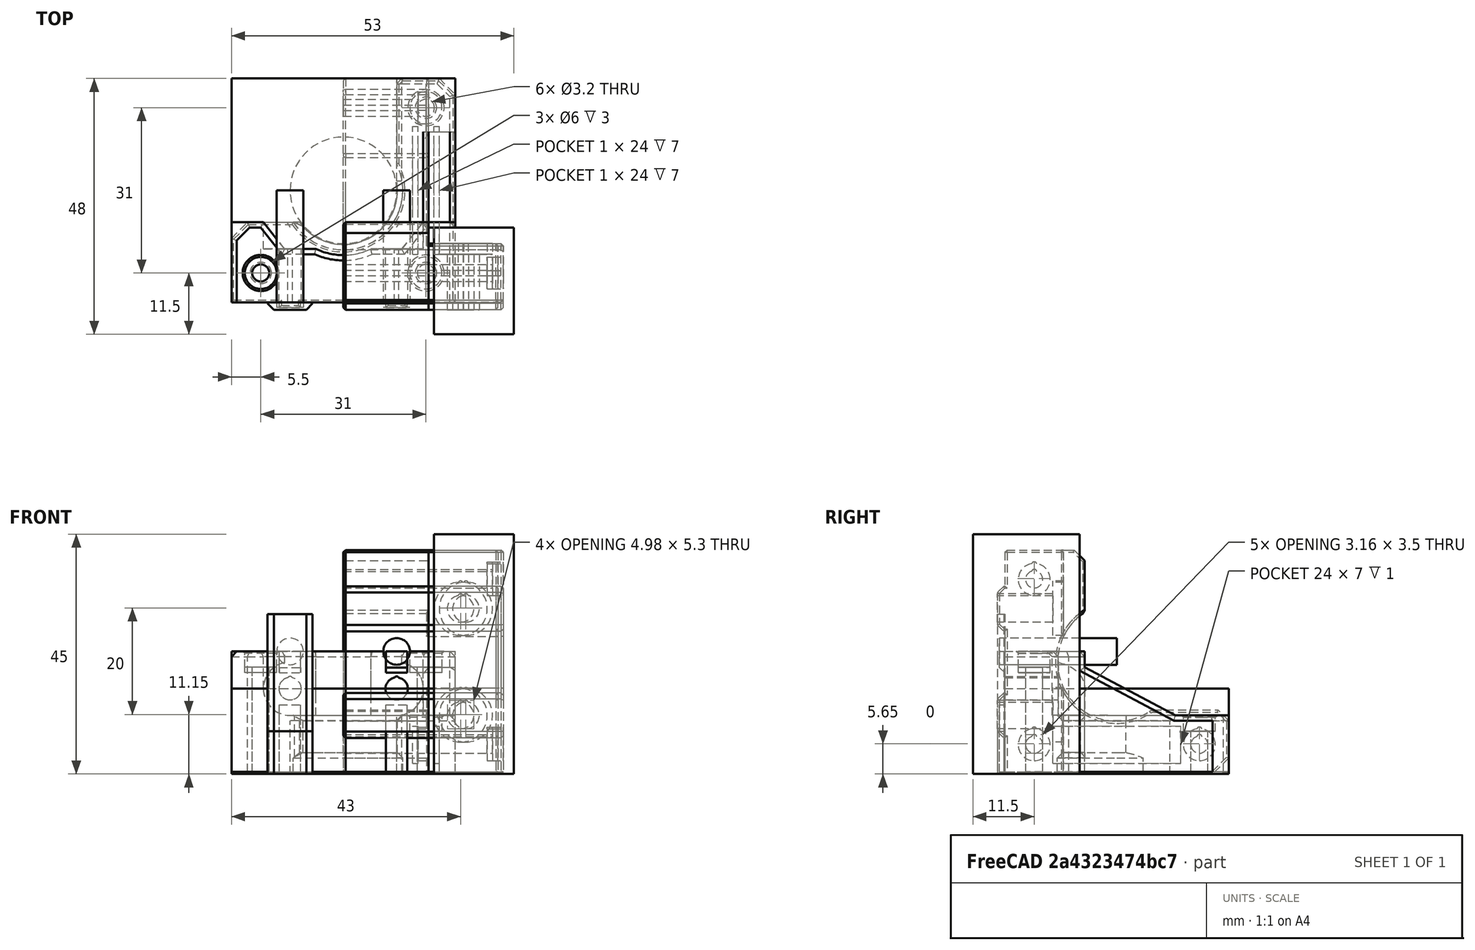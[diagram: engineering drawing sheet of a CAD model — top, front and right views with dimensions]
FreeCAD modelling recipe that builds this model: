
FCSTD DOCUMENT  (FreeCAD 0.18R14555 (Git shallow))
Label: Y-motor-mount
License: All rights reserved
LicenseURL: http://en.wikipedia.org/wiki/All_rights_reserved
objects: Part::Box×22, Part::Cylinder×22, Part::MultiFuse×19, Part::Cut×12, Part::Chamfer×10, Part::Feature×8, Part::MultiCommon×2, Part::Fillet×2
note: 97 computed .brp shape members not serialized (recipe doc carries the construction recipe); baked Part::Feature solids carry a one-line shape summary decoded from their .brp

FEATURE [Part::Box] Box  label="Cube"
  AttacherType = Attacher::AttachEngine3D
  Height = 16
  Length = 42
  Placement = pos=(-21,-21,0) rot=(0,0,1;0rad)
  Width = 42
FEATURE [Part::Cylinder] Cylinder
  Angle = 360
  AttacherType = Attacher::AttachEngine3D
  Height = 4
  Radius = 11.15
FEATURE [Part::Cylinder] Cylinder001
  Angle = 360
  AttacherType = Attacher::AttachEngine3D
  Height = 5
  Placement = pos=(-15.5,-15.5,28) rot=(0,0,1;0rad)
  Radius = 3
FEATURE [Part::Cylinder] Cylinder002
  Angle = 360
  AttacherType = Attacher::AttachEngine3D
  Height = 5
  Placement = pos=(15.5,15.5,8) rot=(0,0,1;0rad)
  Radius = 3
FEATURE [Part::Cylinder] Cylinder003
  Angle = 360
  AttacherType = Attacher::AttachEngine3D
  Height = 5
  Placement = pos=(15.5,-15.5,28) rot=(0,0,1;0rad)
  Radius = 3
FEATURE [Part::Box] Box001  label="Cube001"
  AttacherType = Attacher::AttachEngine3D
  Height = 30
  Length = 42
  Placement = pos=(-21,-21,0) rot=(0,0,1;0rad)
  Width = 15
FEATURE [Part::Box] Box002  label="Cube002"
  AttacherType = Attacher::AttachEngine3D
  Height = 16
  Length = 11
  Placement = pos=(10,-21,0) rot=(0,0,1;0rad)
  Width = 42
FEATURE [Part::Box] Box003  label="Cube003"
  AttacherType = Attacher::AttachEngine3D
  Height = 16
  Length = 42
  Placement = pos=(-21,-21,0) rot=(0,0,1;0rad)
  Width = 15
FEATURE [Part::Cylinder] Cylinder006
  Angle = 360
  AttacherType = Attacher::AttachEngine3D
  Height = 40
  Placement = pos=(-15.5,-15.5,0) rot=(0,0,1;0rad)
  Radius = 1.6
FEATURE [Part::Cylinder] Cylinder007
  Angle = 360
  AttacherType = Attacher::AttachEngine3D
  Height = 40
  Placement = pos=(15.5,-15.5,0) rot=(0,0,1;0rad)
  Radius = 1.6
FEATURE [Part::Cylinder] Cylinder008
  Angle = 360
  AttacherType = Attacher::AttachEngine3D
  Height = 40
  Placement = pos=(15.5,15.5,0) rot=(0,0,1;0rad)
  Radius = 1.6
FEATURE [Part::MultiFuse] Fusion001
  Shapes = -> [Cylinder006,Cylinder007,Cylinder008]
FEATURE [Part::Cylinder] Cylinder011
  Angle = 360
  AttacherType = Attacher::AttachEngine3D
  Height = 22
  Placement = pos=(-10,5.1e-15,23) rot=(1,0,0;1.5708rad)
  Radius = 2.5
FEATURE [Part::Cylinder] Cylinder012
  Angle = 360
  AttacherType = Attacher::AttachEngine3D
  Height = 10
  Placement = pos=(10,-10,23) rot=(1,0,0;1.5708rad)
  Radius = 5
FEATURE [Part::Cylinder] Cylinder013
  Angle = 360
  AttacherType = Attacher::AttachEngine3D
  Height = 22
  Placement = pos=(10,5.1e-15,23) rot=(1,0,0;1.5708rad)
  Radius = 2.5
FEATURE [Part::Cylinder] Cylinder014
  Angle = 360
  AttacherType = Attacher::AttachEngine3D
  Height = 10
  Placement = pos=(-10,-10,23) rot=(1,0,0;1.5708rad)
  Radius = 5
FEATURE [Part::MultiFuse] Fusion003
  Shapes = -> [Cylinder013,Cylinder011]
FEATURE [Part::Feature] Part__Feature  label="y_motor_mount v18"
  shape: bbox 62 x 21 x 44 mm, 162 faces (baked)
FEATURE [Part::Box] Box004  label="Cube004"
  AttacherType = Attacher::AttachEngine3D
  Height = 10
  Length = 10
  Placement = pos=(-15.5,-6,8) rot=(0,0,1;0rad)
  Width = 8
FEATURE [Part::MultiCommon] Common
  Placement = pos=(3.5,-15.5,2) rot=(0.57735,0.57735,-0.57735;4.18879rad)
  Shapes = -> [Part__Feature,Box004]
FEATURE [Part::Feature] Common001
  Placement = pos=(3.5,-15.5,2) rot=(0.57735,0.57735,-0.57735;4.18879rad)
  shape: bbox 8.45 x 1.4 x 8 mm, 8 faces (baked)
FEATURE [Part::Feature] Common002
  Placement = pos=(3.5,-15.5,24) rot=(0.57735,0.57735,-0.57735;4.18879rad)
  shape: bbox 8.45 x 1.4 x 8 mm, 8 faces (baked)
FEATURE [Part::Feature] Common003
  Placement = pos=(3.5,-15.5,16) rot=(0.57735,0.57735,-0.57735;4.18879rad)
  shape: bbox 8.45 x 1.4 x 8 mm, 8 faces (baked)
FEATURE [Part::Feature] Common004
  Placement = pos=(3.5,-15.5,9) rot=(0.57735,0.57735,-0.57735;4.18879rad)
  shape: bbox 8.45 x 1.4 x 8 mm, 8 faces (baked)
FEATURE [Part::MultiFuse] Fusion005
  Shapes = -> [Common002,Common003,Common004,Common001]
FEATURE [Part::Feature] Chamfer002001  label="Chamfer003"
  Placement = pos=(-5e-15,0,21) rot=(0,1,0;1.5708rad)
  shape: bbox 30.28 x 43.4 x 42 mm, 123 faces (baked)
FEATURE [Part::Box] Box005  label="Cube005"
  AttacherType = Attacher::AttachEngine3D
  Height = 45
  Length = 15
  Placement = pos=(17,-27,0) rot=(0,0,1;0rad)
  Width = 20
FEATURE [Part::Feature] Chamfer002002  label="Chamfer004"
  Placement = pos=(-5e-15,0,21) rot=(0,1,0;1.5708rad)
  shape: bbox 30.28 x 43.4 x 42 mm, 123 faces (baked)
FEATURE [Part::Box] Box006  label="Cube006"
  AttacherType = Attacher::AttachEngine3D
  Height = 45
  Length = 15
  Placement = pos=(17,-27,0) rot=(0,0,1;0rad)
  Width = 20
FEATURE [Part::MultiCommon] Common005
  Placement = pos=(-1,0,0) rot=(0,0,1;0rad)
  Shapes = -> [Box006,Chamfer002002]
FEATURE [Part::Cylinder] Cylinder023
  Angle = 360
  AttacherType = Attacher::AttachEngine3D
  Height = 30
  Radius = 10.15
FEATURE [Part::MultiFuse] Fusion005006
  Shapes = -> [Cylinder023,Cylinder]
FEATURE [Part::Chamfer] Chamfer002003
  Base = -> Fusion005006
  Edges = 1 edges r=0.99: [Edge4]
FEATURE [Part::Cylinder] Cylinder024
  Angle = 360
  AttacherType = Attacher::AttachEngine3D
  Height = 39
  Radius = 12.15
FEATURE [Part::Cut] Cut
  Base = -> Box001
  Placement = pos=(0,0,-2) rot=(0,0,1;0rad)
  Tool = -> Cylinder024
FEATURE [Part::Cylinder] Cylinder025
  Angle = 360
  AttacherType = Attacher::AttachEngine3D
  Height = 10
  Radius = 10
FEATURE [Part::MultiFuse] Fusion
  Shapes = -> [Box002,Box003]
FEATURE [Part::Chamfer] Chamfer
  Base = -> Fusion
  Edges = 1 edges r=5: [Edge17]
FEATURE [Part::Cylinder] Cylinder028
  Angle = 360
  AttacherType = Attacher::AttachEngine3D
  Height = 10
  Placement = pos=(10,-20,27.7) rot=(-1,0,0;1.5708rad)
  Radius = 0.5
FEATURE [Part::Cylinder] Cylinder029
  Angle = 360
  AttacherType = Attacher::AttachEngine3D
  Height = 10
  Placement = pos=(-10,-20,27.7) rot=(-1,0,0;1.5708rad)
  Radius = 0.5
FEATURE [Part::MultiFuse] Fusion005008
  Placement = pos=(0,9,-7) rot=(0,0,1;0rad)
  Shapes = -> [Cylinder012,Cylinder028,Cylinder014,Cylinder029]
FEATURE [Part::MultiFuse] Fusion005010
  Placement = pos=(0,0,-8) rot=(0,0,1;0rad)
  Shapes = -> [Cylinder001,Cylinder003]
FEATURE [Part::Box] Box007  label="Cube007"
  AttacherType = Attacher::AttachEngine3D
  Height = 7
  Length = 42
  Placement = pos=(-21,-26,-2) rot=(0,0,1;0rad)
  Width = 47
FEATURE [Part::Box] Box008  label="Cube008"
  AttacherType = Attacher::AttachEngine3D
  Height = 16
  Length = 30
  Placement = pos=(-15,-11,18) rot=(0,0,1;0rad)
  Width = 10
FEATURE [Part::Fillet] Fillet
  Base = -> Box008
  Edges = 2 edges r=5: [Edge4,Edge8]
FEATURE [Part::Box] Box009  label="Cube009"
  AttacherType = Attacher::AttachEngine3D
  Height = 7
  Length = 3
  Placement = pos=(-11,-11,27) rot=(0,0,1;0rad)
  Width = 10
FEATURE [Part::Box] Box010  label="Cube010"
  AttacherType = Attacher::AttachEngine3D
  Height = 7
  Length = 3
  Placement = pos=(8,-11,27) rot=(0,0,1;0rad)
  Width = 10
FEATURE [Part::Box] Box011  label="Cube011"
  AttacherType = Attacher::AttachEngine3D
  Height = 6
  Length = 7
  Placement = pos=(8,-11,28) rot=(0,0,1;0rad)
  Width = 10
FEATURE [Part::Box] Box012  label="Cube012"
  AttacherType = Attacher::AttachEngine3D
  Height = 6
  Length = 7
  Placement = pos=(-15,-11,28) rot=(0,0,1;0rad)
  Width = 10
FEATURE [Part::MultiFuse] Fusion005013
  Shapes = -> [Box012,Box011]
FEATURE [Part::Cut] Cut007
  Base = -> Fillet
  Tool = -> Fusion005013
FEATURE [Part::Fillet] Fillet001
  Base = -> Cut007
  Edges = 2 edges r=4.99: [Edge2,Edge27]
FEATURE [Part::MultiFuse] Fusion005014
  Placement = pos=(0,0,-7) rot=(0,0,1;0rad)
  Shapes = -> [Fillet001,Box009,Box010]
FEATURE [Part::Cylinder] Cylinder030
  Angle = 360
  AttacherType = Attacher::AttachEngine3D
  Height = 20
  Placement = pos=(10,-21,18) rot=(-1,0,0;1.5708rad)
  Radius = 2.1
FEATURE [Part::Cylinder] Cylinder031
  Angle = 360
  AttacherType = Attacher::AttachEngine3D
  Height = 20
  Placement = pos=(-10,-21,18) rot=(-1,0,0;1.5708rad)
  Radius = 2.1
FEATURE [Part::Cylinder] Cylinder032
  Angle = 360
  AttacherType = Attacher::AttachEngine3D
  Height = 20
  Placement = pos=(10,-21,19.8) rot=(-1,0,0;1.5708rad)
  Radius = 0.5
FEATURE [Part::Cylinder] Cylinder033
  Angle = 360
  AttacherType = Attacher::AttachEngine3D
  Height = 20
  Placement = pos=(-10,-21,19.8) rot=(-1,0,0;1.5708rad)
  Radius = 0.5
FEATURE [Part::MultiFuse] Fusion005016
  Placement = pos=(0,0,-2) rot=(0,0,1;0rad)
  Shapes = -> [Cylinder033,Cylinder030,Cylinder032,Cylinder031]
FEATURE [Part::Box] Box014  label="Cube014"
  AttacherType = Attacher::AttachEngine3D
  Height = 13
  Length = 4
  Placement = pos=(8,-22,0) rot=(0,0,1;0rad)
  Width = 1
FEATURE [Part::Box] Box015  label="Cube015"
  AttacherType = Attacher::AttachEngine3D
  Height = 13
  Length = 4
  Placement = pos=(-12,-22,0) rot=(0,0,1;0rad)
  Width = 1
FEATURE [Part::Box] Box016  label="Cube016"
  AttacherType = Attacher::AttachEngine3D
  Height = 4
  Length = 4
  Placement = pos=(8,-22,21) rot=(0,0,1;0rad)
  Width = 1
FEATURE [Part::Box] Box017  label="Cube017"
  AttacherType = Attacher::AttachEngine3D
  Height = 4
  Length = 4
  Placement = pos=(-12,-22,21) rot=(0,0,1;0rad)
  Width = 1
FEATURE [Part::Chamfer] Chamfer002006
  Base = -> Box017
  Edges = 1 edges r=0.99: [Edge9]
  Placement = pos=(0,0,-2) rot=(0,0,1;0rad)
FEATURE [Part::Chamfer] Chamfer002007
  Base = -> Box016
  Edges = 1 edges r=0.99: [Edge9]
  Placement = pos=(0,0,-2) rot=(0,0,1;0rad)
FEATURE [Part::Box] Box018  label="Cube018"
  AttacherType = Attacher::AttachEngine3D
  Height = 7
  Length = 1
  Placement = pos=(13,-12,2) rot=(0,0,1;0rad)
  Width = 24
FEATURE [Part::Box] Box019  label="Cube019"
  AttacherType = Attacher::AttachEngine3D
  Height = 7
  Length = 1
  Placement = pos=(17,-12,2) rot=(0,0,1;0rad)
  Width = 24
FEATURE [Part::MultiFuse] Fusion005018002  label="selective-infill"
  Shapes = -> [Box018,Box019]
FEATURE [Part::MultiFuse] Fusion005018004
  Shapes = -> [Chamfer,Cut]
FEATURE [Part::Cut] Cut008
  Base = -> Fusion005018004
  Placement = pos=(0,0,-5) rot=(0,0,1;0rad)
  Tool = -> Box007
FEATURE [Part::Cut] Cut009
  Base = -> Cut008
  Tool = -> Chamfer002003
FEATURE [Part::Cut] Cut010
  Base = -> Cut009
  Tool = -> Cylinder002
FEATURE [Part::Cut] Cut011
  Base = -> Cut010
  Tool = -> Fusion005010
FEATURE [Part::Cut] Cut012
  Base = -> Cut011
  Tool = -> Fusion001
FEATURE [Part::Cut] Cut013
  Base = -> Cut012
  Tool = -> Fusion005008
FEATURE [Part::Cut] Cut014
  Base = -> Cut013
  Tool = -> Fusion005016
FEATURE [Part::Box] Box020  label="Cube020"
  AttacherType = Attacher::AttachEngine3D
  Height = 10
  Length = 6
  Placement = pos=(15,-7,10) rot=(0,0,1;0rad)
  Width = 18
FEATURE [Part::Box] Box021  label="Cube021"
  AttacherType = Attacher::AttachEngine3D
  Height = 10
  Length = 10
  Placement = pos=(5,-11,16) rot=(0,0,1;0rad)
  Width = 10
FEATURE [Part::Box] Box022  label="Cube022"
  AttacherType = Attacher::AttachEngine3D
  Height = 10
  Length = 10
  Placement = pos=(-15,-11,16) rot=(0,0,1;0rad)
  Width = 10
FEATURE [Part::Chamfer] Chamfer002010
  Base = -> Box021
  Edges = 1 edges: [Edge5 r1=5 r2=4]
FEATURE [Part::Chamfer] Chamfer002011
  Base = -> Box022
  Edges = 1 edges: [Edge1 r1=5 r2=4]
FEATURE [Part::MultiFuse] Fusion005018006002
  Shapes = -> [Chamfer002010,Chamfer002011]
FEATURE [Part::MultiFuse] Fusion005018006003
  Shapes = -> [Fusion005018006002]
FEATURE [Part::MultiFuse] Fusion005018006004
  Shapes = -> [Fusion005018006003]
FEATURE [Part::MultiFuse] Fusion005018006005
  Shapes = -> [Fusion005018006004,Fusion005014]
FEATURE [Part::MultiFuse] Fusion005018006006
  Shapes = -> [Box014,Box015,Chamfer002006,Chamfer002007]
FEATURE [Part::Cut] Cut015
  Base = -> Cut014
  Tool = -> Fusion005018006005
FEATURE [Part::Chamfer] Chamfer002012
  Base = -> Box020
  Edges = 1 edges: [Edge12 r1=9 r2=17]
FEATURE [Part::MultiFuse] Fusion005018006007
  Shapes = -> [Fusion005018006006,Cut015,Chamfer002012]
FEATURE [Part::Feature] Fusion005018006007001  label="Fusion005018006008"
  shape: bbox 42 x 43 x 23 mm, 61 faces (baked)
FEATURE [Part::Chamfer] Chamfer002013
  Base = -> Fusion005018006007001
  Edges = 2 edges r=3: [Edge90,Edge151]
FEATURE [Part::Chamfer] Chamfer002014
  Base = -> Chamfer002013
  Edges = 23 edges r=1: [Edge22,Edge26,Edge50,Edge55,Edge67,Edge68,Edge72,Edge77,Edge80,Edge81,Edge82,Edge83,Edge91,Edge92,Edge93,Edge95,Edge97,Edge99,Edge142,Edge143,Edge144,Edge145,Edge159]
FEATURE [Part::Chamfer] Chamfer002015
  Base = -> Chamfer002014
  Edges = 25 edges r=0.4: [Edge1,Edge2,Edge3,Edge4,Edge5,Edge6,Edge7,Edge8,Edge9,Edge10,Edge11,Edge12,Edge13,Edge14,Edge15,Edge16,Edge17,Edge18,Edge19,Edge20,Edge21,Edge22,Edge145,Edge168,Edge169]
FEATURE [Part::Cut] Cut016
  Base = -> Chamfer002015
  Tool = -> Fusion005018002
FEATURE [Part::Cylinder] Cylinder034
  Angle = 360
  AttacherType = Attacher::AttachEngine3D
  Height = 4
  Placement = pos=(15.5,-15.5,19) rot=(0,0,1;0rad)
  Radius = 3
FEATURE [Part::Cylinder] Cylinder035
  Angle = 360
  AttacherType = Attacher::AttachEngine3D
  Height = 4
  Placement = pos=(-15.5,-15.5,19) rot=(0,0,1;0rad)
  Radius = 3
FEATURE [Part::MultiFuse] Fusion005018006007002  label="bolt-slot-extra"
  Shapes = -> [Cylinder035,Cylinder034]
FEATURE [Part::Cut] Cut017
  Base = -> Cut016
  Tool = -> Fusion005018006007002
